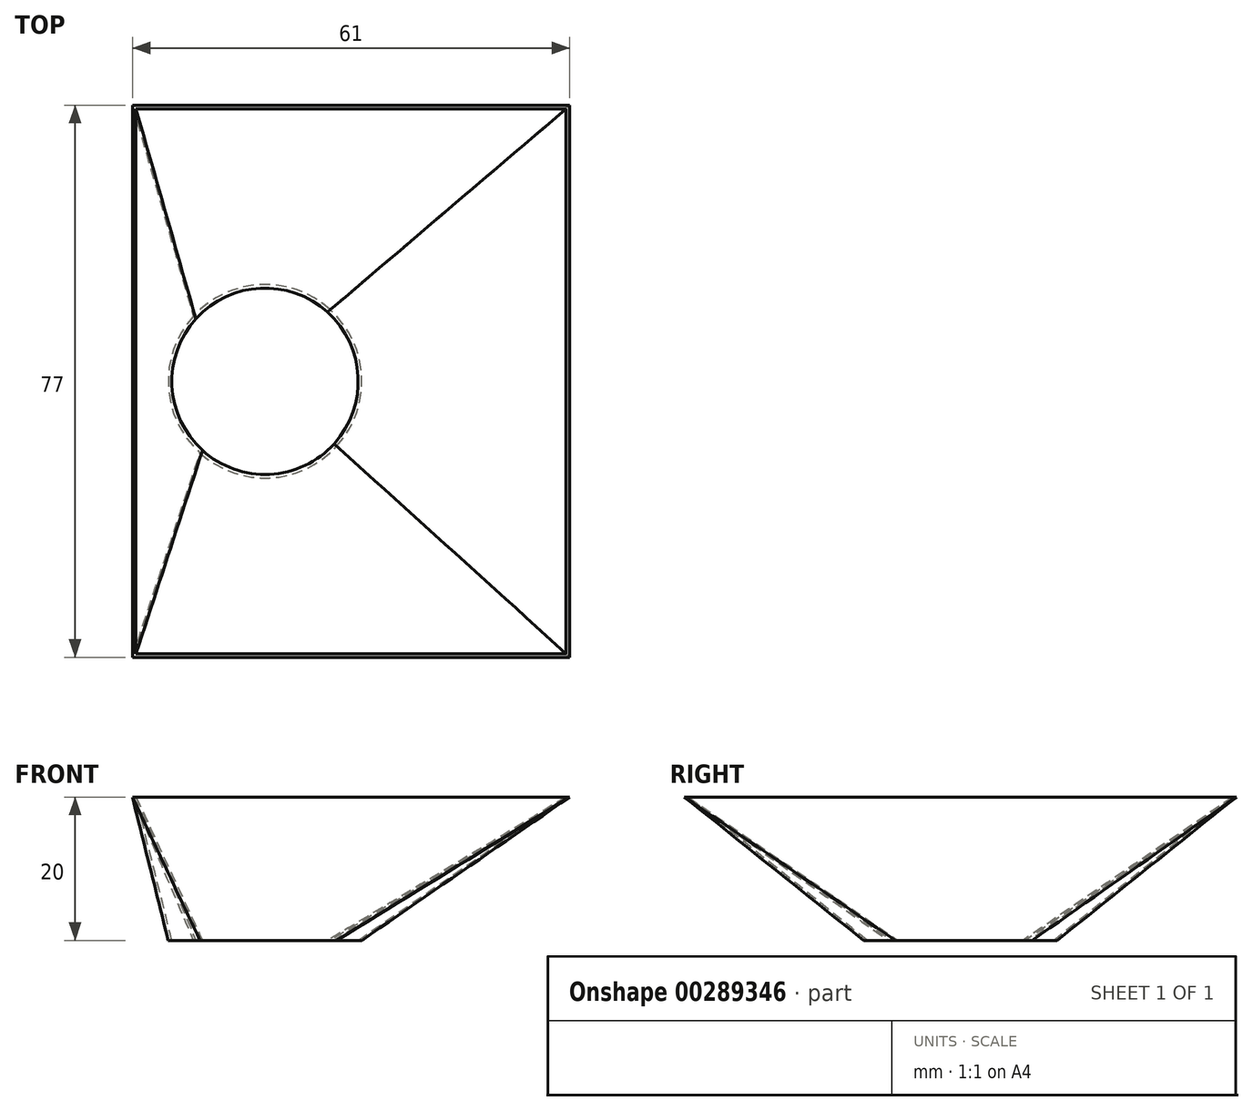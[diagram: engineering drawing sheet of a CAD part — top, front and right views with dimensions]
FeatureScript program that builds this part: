
annotation { "Feature Type Name" : "Feature", "Feature Type Description" : "" }
export const myFeature = defineFeature(function(context is Context, id is Id, definition is map)
    precondition{}
    {
        {
            var Q0;
            Q0=qCreatedBy(makeId("Top.planeOp"),FACE);
            var sketch = newSketch(context, id + "F0", { "sketchPlane" : qUnion([Q0]) });
            skCircle(sketch, "E0", {"center": v(0, 0) * mm, "radius": 13.5 * mm});
            skSolve(sketch);
        }
        {
            var Q0;
            Q0=qCreatedBy(makeId("Top.planeOp"),FACE);
            cPlane(context, id + "F1", {"entities" : qUnion([Q0]), "cplaneType" : CPlaneType.OFFSET, "offset" : 20 * mm, "width" : 150 * mm, "height" : 150 * mm});
        }
        {
            var Q0;
            Q0=qCreatedBy(id+"F1.planeOp",FACE);
            var sketch = newSketch(context, id + "F2", { "sketchPlane" : qUnion([Q0]) });
            skLineSegment(sketch, "E1.bottom", {"start": v(42.5, -38.5) * mm, "end": v(-18.5, -38.5) * mm});
            skLineSegment(sketch, "E1.top", {"start": v(42.5, 38.5) * mm, "end": v(-18.5, 38.5) * mm});
            skLineSegment(sketch, "E1.left", {"start": v(42.5, -38.5) * mm, "end": v(42.5, 38.5) * mm});
            skLineSegment(sketch, "E1.right", {"start": v(-18.5, -38.5) * mm, "end": v(-18.5, 38.5) * mm});
            skPoint(sketch, "E1.middle", {"position": v(12, 0) * mm});
            skSolve(sketch);
        }
        {
            var Q0;
            Q0=qSketchRegion(id+"F2",true);
            var Q1;
            Q1=qSketchRegion(id+"F0",true);
            loft(context, id + "F3", {"sheetProfilesArray" : [{ "sheetProfileEntities" : qUnion([Q0]) }, { "sheetProfileEntities" : qUnion([Q1]) }]});
        }
        {
            var Q0;
            Q0=makeQuery(id+"F3.opLoft","CAP_FACE",FACE,{"disambiguationData":[OSD([makeQuery(id+"F0.imprint","IMPRINT",FACE,{"disambiguationData":[TD([[makeQuery(id+"F0.imprint","IMPRINT",EDGE,{"derivedFrom":sQuery(id+"F0.wireOp",EDGE,"E0")}),1.0]])]})])],"isStart":true});
            var sketch = newSketch(context, id + "F4", { "sketchPlane" : qUnion([Q0]) });
            skCircle(sketch, "E2", {"center": v(0, 0) * mm, "radius": 13 * mm});
            skSolve(sketch);
        }
        {
            var Q0;
            Q0=makeQuery(id+"F3.opLoft","CAP_FACE",FACE,{"disambiguationData":[OSD([makeQuery(id+"F2.imprint","IMPRINT",FACE,{"disambiguationData":[TD([[makeQuery(id+"F2.imprint","IMPRINT",EDGE,{"derivedFrom":sQuery(id+"F2.wireOp",EDGE,"E1.bottom")}),-1.0]])]})])],"isStart":true});
            var sketch = newSketch(context, id + "F5", { "sketchPlane" : qUnion([Q0]) });
            skLineSegment(sketch, "E3.bottom", {"start": v(42, -38) * mm, "end": v(-18, -38) * mm});
            skLineSegment(sketch, "E3.top", {"start": v(42, 38) * mm, "end": v(-18, 38) * mm});
            skLineSegment(sketch, "E3.left", {"start": v(42, -38) * mm, "end": v(42, 38) * mm});
            skLineSegment(sketch, "E3.right", {"start": v(-18, -38) * mm, "end": v(-18, 38) * mm});
            skPoint(sketch, "E3.middle", {"position": v(12, 0) * mm});
            skSolve(sketch);
        }
        {
            var Q1;
            Q1=qSketchRegion(id+"F5",true);
            var Q2;
            Q2=qSketchRegion(id+"F4",true);
            loft(context, id + "F6", {"operationType" : NewBodyOperationType.REMOVE, "sheetProfilesArray" : [{ "sheetProfileEntities" : qUnion([Q1]) }, { "sheetProfileEntities" : qUnion([Q2]) }]});
        }
    });
